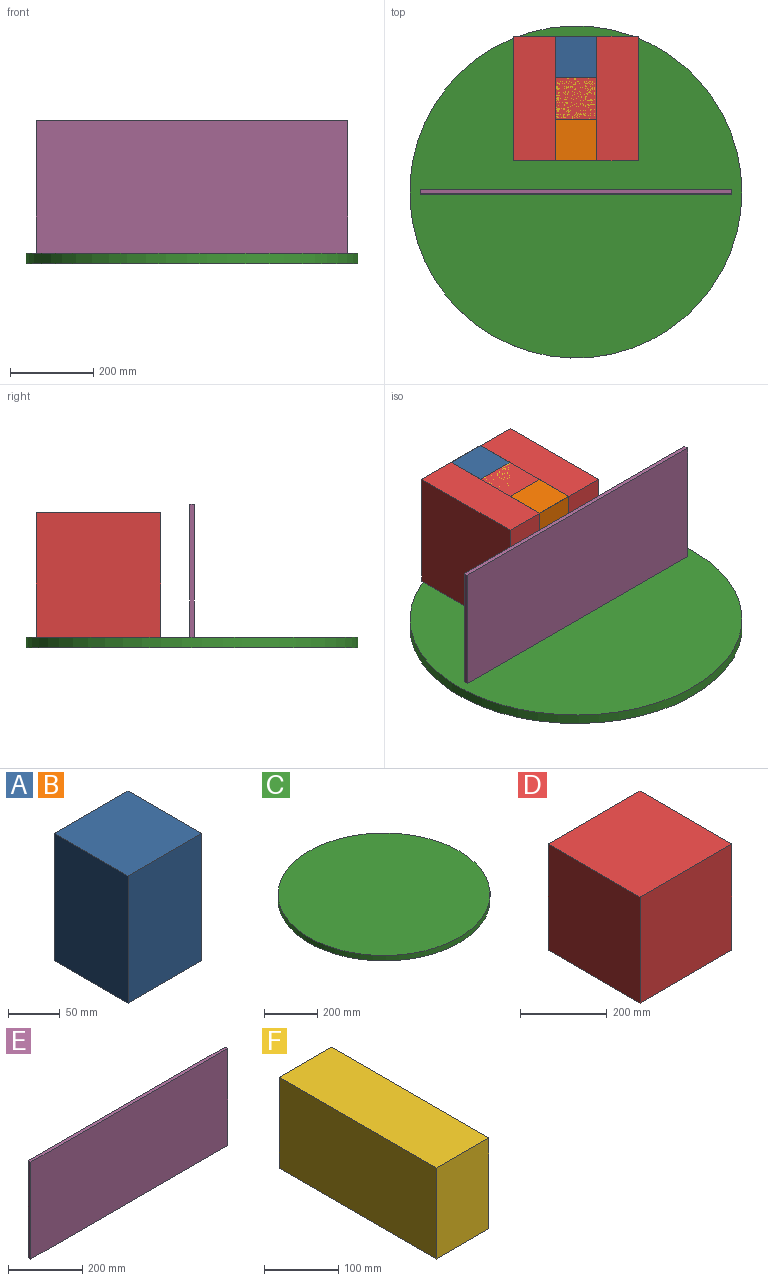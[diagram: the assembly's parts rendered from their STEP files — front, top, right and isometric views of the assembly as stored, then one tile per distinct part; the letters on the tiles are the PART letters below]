
ASSEMBLY  parts=6 mates=5
PART A: 6 faces, bbox 100x100x150 mm
  f0: plane 150x100mm, normal (-1,0,0), area 15000mm2, adj f1,f3,f4,f5
  f1: plane 150x100mm, normal (0,-1,0), area 15000mm2, adj f0,f2,f4,f5
  f2: plane 150x100mm, normal (1,0,0), area 15000mm2, adj f1,f3,f4,f5
  f3: plane 150x100mm, normal (0,1,0), area 15000mm2, adj f0,f2,f4,f5
  f4: plane 100x100mm, normal (0,0,1), area 10000mm2, adj f0,f1,f2,f3
  f5: plane 100x100mm, normal (0,0,-1), area 10000mm2, adj f0,f1,f2,f3
PART B: same geometry as A
PART C: 3 faces, bbox 800x800x25 mm
  f0: cylinder r=400mm len=800mm, axis (0,0,-1), area 62831.9mm2, adj f1,f2
  f1: plane 800x800mm, normal (0,0,1), area 502654.8mm2, adj f0
  f2: plane 800x800mm, normal (0,0,-1), area 502654.8mm2, adj f0
PART D: 6 faces, bbox 300x300x300 mm
  f0: plane 300x300mm, normal (-1,0,0), area 90000mm2, adj f1,f3,f4,f5
  f1: plane 300x300mm, normal (0,-1,0), area 90000mm2, adj f0,f2,f4,f5
  f2: plane 300x300mm, normal (1,0,0), area 90000mm2, adj f1,f3,f4,f5
  f3: plane 300x300mm, normal (0,1,0), area 90000mm2, adj f0,f2,f4,f5
  f4: plane 300x300mm, normal (0,0,1), area 90000mm2, adj f0,f1,f2,f3
  f5: plane 300x300mm, normal (0,0,-1), area 90000mm2, adj f0,f1,f2,f3
PART E: 6 faces, bbox 750x10x320 mm
  f0: plane 320x10mm, normal (-1,0,0), area 3200mm2, adj f1,f3,f4,f5
  f1: plane 750x320mm, normal (0,-1,0), area 240000mm2, adj f0,f2,f4,f5
  f2: plane 320x10mm, normal (1,0,0), area 3200mm2, adj f1,f3,f4,f5
  f3: plane 750x320mm, normal (0,1,0), area 240000mm2, adj f0,f2,f4,f5
  f4: plane 750x10mm, normal (0,0,1), area 7500mm2, adj f0,f1,f2,f3
  f5: plane 750x10mm, normal (0,0,-1), area 7500mm2, adj f0,f1,f2,f3
PART F: 6 faces, bbox 100x300x150 mm
  f0: plane 300x150mm, normal (-1,0,0), area 45000mm2, adj f1,f3,f4,f5
  f1: plane 150x100mm, normal (0,-1,0), area 15000mm2, adj f0,f2,f4,f5
  f2: plane 300x150mm, normal (1,0,0), area 45000mm2, adj f1,f3,f4,f5
  f3: plane 150x100mm, normal (0,1,0), area 15000mm2, adj f0,f2,f4,f5
  f4: plane 300x100mm, normal (0,0,1), area 30000mm2, adj f0,f1,f2,f3
  f5: plane 300x100mm, normal (0,0,-1), area 30000mm2, adj f0,f1,f2,f3
PLACE A t=(-50,275,175)mm
PLACE B t=(-50,75,175)mm
PLACE C at identity fixed
PLACE D t=(-150,75,25)mm
PLACE E t=(-375,-5,25)mm
PLACE F t=(-50,75,175)mm
MATE planar C.f0 <-> D.f5  axis (0,0,1) through (0,0,25)mm
MATE planar F.f4 <-> B.f4  axis (0,0,1) through (0,75,325)mm
MATE planar D.f4 <-> F.f4  axis (0,0,1) through (0,225,325)mm
MATE planar F.f4 <-> A.f4  axis (0,0,1) through (0,375,325)mm
MATE planar C.f0 <-> E.f5  axis (0,0,1) through (0,0,25)mm
